# Revit family: PowderCoatRange_Dulux_Duralloy
name_source: partatom
category: Generic Models
revit_build: Autodesk Revit 2018 (Build: 20190510_1515(x64)
units: mm (PartAtom-declared; Revit-internal decimal feet)

## family parameters
Always vertical = Yes
Can host rebar = No
Cut with Voids When Loaded = No
Part Type = Normal
Room Calculation Point = No
Round Connector Dimension = Use Diameter
Shared = No
Work Plane-Based = No

## types (1)
- PowderCoatRange_Dulux_Duralloy
    Manufacturer = Dulux
    Material0001 = PowderCoat_Dulux_Duralloy_Almond_Matt
    Material0002 = PowderCoat_Dulux_Duralloy_ApplianceWhite_Matt
    Material0003 = PowderCoat_Dulux_Duralloy_Aquarium_Matt
    Material0004 = PowderCoat_Dulux_Duralloy_ArcticWhite_Satin
    Material0005 = PowderCoat_Dulux_Duralloy_Azure_Matt
    Material0006 = PowderCoat_Dulux_Duralloy_BlueFin_Matt
    Material0007 = PowderCoat_Dulux_Duralloy_Blueseye_Matt
    Material0008 = PowderCoat_Dulux_Duralloy_BondRivergum_Matt
    Material0009 = PowderCoat_Dulux_Duralloy_BoneWhite_Matt
    Material0010 = PowderCoat_Dulux_Duralloy_Bronco_Matt
    Material0011 = PowderCoat_Dulux_Duralloy_CanvasCloth_Matt
    Material0012 = PowderCoat_Dulux_Duralloy_ChampagneKinetic_Matt
    Material0013 = PowderCoat_Dulux_Duralloy_ChampersKinetic_Matt
    Material0014 = PowderCoat_Dulux_Duralloy_Charcoal_Matt
    Material0015 = PowderCoat_Dulux_Duralloy_ColaRed_Satin
    Material0016 = PowderCoat_Dulux_Duralloy_CopperMetallicKinetic_Satin
    Material0017 = PowderCoat_Dulux_Duralloy_DeepTeal_Matt
    Material0018 = PowderCoat_Dulux_Duralloy_DesertSand_Matt
    Material0019 = PowderCoat_Dulux_Duralloy_Dijon_Matt
    Material0020 = PowderCoat_Dulux_Duralloy_Flaxpod_Matt
    Material0021 = PowderCoat_Dulux_Duralloy_Flint_Matt
    Material0022 = PowderCoat_Dulux_Duralloy_GhostGrey_Matt
    Material0023 = PowderCoat_Dulux_Duralloy_Gravel_Matt
    Material0024 = PowderCoat_Dulux_Duralloy_GreyFriars_Matt
    Material0025 = PowderCoat_Dulux_Duralloy_GullGrey_Matt
    Material0026 = PowderCoat_Dulux_Duralloy_GunmetalMetallicKinetic_Satin
    Material0027 = PowderCoat_Dulux_Duralloy_IndigoBlue_Matt
    Material0028 = PowderCoat_Dulux_Duralloy_Ironsand_Matt
    Material0029 = PowderCoat_Dulux_Duralloy_Jay_Matt
    Material0030 = PowderCoat_Dulux_Duralloy_Karaka_Matt
    Material0031 = PowderCoat_Dulux_Duralloy_Kauri_Matt
    Material0032 = PowderCoat_Dulux_Duralloy_Kodiak_Matt
    Material0033 = PowderCoat_Dulux_Duralloy_Lichen_Matt
    Material0034 = PowderCoat_Dulux_Duralloy_Lignite_Matt
    Material0035 = PowderCoat_Dulux_Duralloy_Magnolia_Matt
    Material0036 = PowderCoat_Dulux_Duralloy_MannexApplianceWhite_Matt
    Material0037 = PowderCoat_Dulux_Duralloy_MannexBronco_Matt
    Material0038 = PowderCoat_Dulux_Duralloy_MannexCharcoal_Matt
    Material0039 = PowderCoat_Dulux_Duralloy_MannexGreyFriars_Matt
    Material0040 = PowderCoat_Dulux_Duralloy_MannexIronsand_Matt
    Material0041 = PowderCoat_Dulux_Duralloy_MannexBlack_Matt
    Material0042 = PowderCoat_Dulux_Duralloy_MannexMetroSilverPearl_Matt
    Material0043 = PowderCoat_Dulux_Duralloy_MannexSandstoneGrey_Matt
    Material0044 = PowderCoat_Dulux_Duralloy_MannexTitania_Matt
    Material0045 = PowderCoat_Dulux_Duralloy_Black_Matt
    Material0046 = PowderCoat_Dulux_Duralloy_MetropolisCoalDustKinetic_Matt
    Material0047 = PowderCoat_Dulux_Duralloy_MetropolisElectricCowKinetic_Matt
    Material0048 = PowderCoat_Dulux_Duralloy_MetropolisSilverPearlKinetic_Satin
    Material0049 = PowderCoat_Dulux_Duralloy_MetropolisWarmWhitePearlKinetic_Satin
    Material0050 = PowderCoat_Dulux_Duralloy_MidGrey_Matt
    Material0051 = PowderCoat_Dulux_Duralloy_MineralBrownKinetic_Satin
    Material0052 = PowderCoat_Dulux_Duralloy_MistGreen_Matt
    Material0053 = PowderCoat_Dulux_Duralloy_Navy_Matt
    Material0054 = PowderCoat_Dulux_Duralloy_NewDenimBlue_Matt
    Material0055 = PowderCoat_Dulux_Duralloy_Oceans12Kinetic_Satin
    Material0056 = PowderCoat_Dulux_Duralloy_OffWhite_Matt
    Material0057 = PowderCoat_Dulux_Duralloy_O'KeefeGrey_Matt
    Material0058 = PowderCoat_Dulux_Duralloy_Olive_Matt
    Material0059 = PowderCoat_Dulux_Duralloy_PermanentGreen_Matt
    Material0060 = PowderCoat_Dulux_Duralloy_PioneerRed_Matt
    Material0061 = PowderCoat_Dulux_Duralloy_PlatypusKinetic_Satin
    Material0062 = PowderCoat_Dulux_Duralloy_Pohutukawa_Matt
    Material0063 = PowderCoat_Dulux_Duralloy_Pounamu_Matt
    Material0064 = PowderCoat_Dulux_Duralloy_RangoonGreen_Matt
    Material0065 = PowderCoat_Dulux_Duralloy_RivergumBeige_Matt
    Material0066 = PowderCoat_Dulux_Duralloy_SandstoneGrey_Matt
    Material0067 = PowderCoat_Dulux_Duralloy_Black_Satin
    Material0068 = PowderCoat_Dulux_Duralloy_Scoria_Matt
    Material0069 = PowderCoat_Dulux_Duralloy_SilverStarKinetic_Satin
    Material0070 = PowderCoat_Dulux_Duralloy_SlateBlue_Matt
    Material0071 = PowderCoat_Dulux_Duralloy_SmoothCream_Matt
    Material0072 = PowderCoat_Dulux_Duralloy_Sorrell_Matt
    Material0073 = PowderCoat_Dulux_Duralloy_StElmosFireKinetic_Satin
    Material0074 = PowderCoat_Dulux_Duralloy_Stone_Matt
    Material0075 = PowderCoat_Dulux_Duralloy_StormBlue_Matt
    Material0076 = PowderCoat_Dulux_Duralloy_Stromboli_Matt
    Material0077 = PowderCoat_Dulux_Duralloy_Terracotta_Matt
    Material0078 = PowderCoat_Dulux_Duralloy_ThunderGrey_Matt
    Material0079 = PowderCoat_Dulux_Duralloy_Titania_Matt
    Material0080 = PowderCoat_Dulux_Duralloy_Tomcat_Matt
    Material0081 = PowderCoat_Dulux_Duralloy_TransformerGrey_Matt
    Material0082 = PowderCoat_Dulux_Duralloy_TuataraKintetic_Satin
    Material0083 = PowderCoat_Dulux_Duralloy_TuskTusk_Matt
    Material0084 = PowderCoat_Dulux_Duralloy_Wasp_Matt
    Material0085 = PowderCoat_Dulux_Duralloy_Wedgewood_Matt
    Material0086 = PowderCoat_Dulux_Duralloy_WindowBronzeKinetic_Matt
    Material0087 = PowderCoat_Dulux_Duralloy_Wizard_Matt
    Material0088 = PowderCoat_Dulux_Duralloy_Woodwind_Matt
    Material0089 = <By Category>
    Material0090 = <By Category>
    Material0091 = <By Category>
    Material0092 = <By Category>
    Material0093 = <By Category>
    Material0094 = <By Category>
    Material0095 = <By Category>
    Material0096 = <By Category>
    Material0097 = <By Category>
    Material0098 = <By Category>
    Material0099 = <By Category>
    Material0100 = <By Category>
    Material0101 = <By Category>
    Material0102 = <By Category>
    Material0103 = <By Category>
    Material0104 = <By Category>
    Material0105 = <By Category>
    Material0106 = <By Category>
    Material0107 = <By Category>
    Material0108 = <By Category>
    Material0109 = <By Category>
    Material0110 = <By Category>
    Material0111 = <By Category>
    Material0112 = <By Category>
    Material0113 = <By Category>
    Material0114 = <By Category>
    Material0115 = <By Category>
    Material0116 = <By Category>
    Material0117 = <By Category>
    Material0118 = <By Category>
    Material0119 = <By Category>
    Material0120 = <By Category>
    Material0121 = <By Category>
    Material0122 = <By Category>
    Material0123 = <By Category>
    Material0124 = <By Category>
    Material0125 = <By Category>
    Material0126 = <By Category>
    Material0127 = <By Category>
    Material0128 = <By Category>
    Material0129 = <By Category>
    Material0130 = <By Category>
    Material0131 = <By Category>
    Material0132 = <By Category>
    Material0133 = <By Category>
    Material0134 = <By Category>
    Material0135 = <By Category>
    Material0136 = <By Category>
    Material0137 = <By Category>
    Material0138 = <By Category>
    Material0139 = <By Category>
    Material0140 = <By Category>
    Material0141 = <By Category>
    Material0142 = <By Category>
    Material0143 = <By Category>
    Material0144 = <By Category>
    Material0145 = <By Category>
    Material0146 = <By Category>
    Material0147 = <By Category>
    Material0148 = <By Category>
    Material0149 = <By Category>
    Material0150 = <By Category>
    Material0151 = <By Category>
    Material0152 = <By Category>
    Material0153 = <By Category>
    Material0154 = <By Category>
    Material0155 = <By Category>
    Material0156 = <By Category>
    Material0157 = <By Category>
    Material0158 = <By Category>
    Material0159 = <By Category>
    Material0160 = <By Category>
    Material0161 = <By Category>
    Material0162 = <By Category>
    Material0163 = <By Category>
    Material0164 = <By Category>
    Material0165 = <By Category>
    Material0166 = <By Category>
    Material0167 = <By Category>
    Material0168 = <By Category>
    Material0169 = <By Category>
    Material0170 = <By Category>
    Material0171 = <By Category>
    Material0172 = <By Category>
    Material0173 = <By Category>
    Material0174 = <By Category>
    Material0175 = <By Category>
    Material0176 = <By Category>
    Material0177 = <By Category>
    Material0178 = <By Category>
    Material0179 = <By Category>
    Material0180 = <By Category>
    Material0181 = <By Category>
    Material0182 = <By Category>
    Material0183 = <By Category>
    Material0184 = <By Category>
    Material0185 = <By Category>
    Material0186 = <By Category>
    Material0187 = <By Category>
    Material0188 = <By Category>
    Material0189 = <By Category>
    Material0190 = <By Category>
    Material0191 = <By Category>
    Material0192 = <By Category>
    Material0193 = <By Category>
    Material0194 = <By Category>
    Material0195 = <By Category>
    Material0196 = <By Category>
    Material0197 = <By Category>
    Material0198 = <By Category>
    Material0199 = <By Category>
    Material0200 = <By Category>
    Material0201 = <By Category>
    Material0202 = <By Category>
    Material0203 = <By Category>
    Material0204 = <By Category>
    Material0205 = <By Category>
    Material0206 = <By Category>
    Material0207 = <By Category>
    Material0208 = <By Category>
    Material0209 = <By Category>
    Material0210 = <By Category>
    Material0211 = <By Category>
    Material0212 = <By Category>
    Material0213 = <By Category>
    Material0214 = <By Category>
    Material0215 = <By Category>
    Material0216 = <By Category>
    Material0217 = <By Category>
    Material0218 = <By Category>
    Material0219 = <By Category>
    Material0220 = <By Category>
    Material0221 = <By Category>
    Material0222 = <By Category>
    Material0223 = <By Category>
    Material0224 = <By Category>
    Material0225 = <By Category>
    Material0226 = <By Category>
    Material0227 = <By Category>
    Material0228 = <By Category>
    Material0229 = <By Category>
    Material0230 = <By Category>
    Material0231 = <By Category>
    Material0232 = <By Category>
    Material0233 = <By Category>
    Material0234 = <By Category>
    Material0235 = <By Category>
    Material0236 = <By Category>
    Material0237 = <By Category>
    Material0238 = <By Category>
    Material0239 = <By Category>
    Material0240 = <By Category>
    Material0241 = <By Category>
    Material0242 = <By Category>
    Material0243 = <By Category>
    Material0244 = <By Category>
    Material0245 = <By Category>
    Material0246 = <By Category>
    Material0247 = <By Category>
    Material0248 = <By Category>
    Material0249 = <By Category>
    Material0250 = <By Category>
    Material0251 = <By Category>
    Material0252 = <By Category>
    Material0253 = <By Category>
    Material0254 = <By Category>
    Material0255 = <By Category>
    Material0256 = <By Category>
    Material0257 = <By Category>
    Material0258 = <By Category>
    Material0259 = <By Category>
    Material0260 = <By Category>
    Material0261 = <By Category>
    Material0262 = <By Category>
    Material0263 = <By Category>
    Material0264 = <By Category>
    Material0265 = <By Category>
    Material0266 = <By Category>
    Material0267 = <By Category>
    Material0268 = <By Category>
    Material0269 = <By Category>
    Material0270 = <By Category>
    Material0271 = <By Category>
    Material0272 = <By Category>
    Material0273 = <By Category>
    Material0274 = <By Category>
    Material0275 = <By Category>
    Material0276 = <By Category>
    Material0277 = <By Category>
    Material0278 = <By Category>
    Material0279 = <By Category>
    Material0280 = <By Category>
    Material0281 = <By Category>
    Material0282 = <By Category>
    Material0283 = <By Category>
    Material0284 = <By Category>
    Material0285 = <By Category>
    Material0286 = <By Category>
    Material0287 = <By Category>
    Material0288 = <By Category>
    Material0289 = <By Category>
    Material0290 = <By Category>
    Material0291 = <By Category>
    Material0292 = <By Category>
    Material0293 = <By Category>
    Material0294 = <By Category>
    Material0295 = <By Category>
    Material0296 = <By Category>
    Material0297 = <By Category>
    Material0298 = <By Category>
    Material0299 = <By Category>
    Material0300 = <By Category>
    Material0301 = <By Category>
    Material0302 = <By Category>
    Material0303 = <By Category>
    Material0304 = <By Category>
    Material0305 = <By Category>
    Material0306 = <By Category>
    Material0307 = <By Category>
    Material0308 = <By Category>
    Material0309 = <By Category>
    Material0310 = <By Category>
    Material0311 = <By Category>
    Material0312 = <By Category>
    Material0313 = <By Category>
    Material0314 = <By Category>
    Material0315 = <By Category>
    Material0316 = <By Category>
    Material0317 = <By Category>
    Material0318 = <By Category>
    Material0319 = <By Category>
    Material0320 = <By Category>
    Material0321 = <By Category>
    Material0322 = <By Category>
    Material0323 = <By Category>
    Material0324 = <By Category>
    Material0325 = <By Category>
    Material0326 = <By Category>
    Material0327 = <By Category>
    Material0328 = <By Category>
    Material0329 = <By Category>
    Material0330 = <By Category>
    Material0331 = <By Category>
    Material0332 = <By Category>
    Material0333 = <By Category>
    Material0334 = <By Category>
    Material0335 = <By Category>
    Material0336 = <By Category>
    Material0337 = <By Category>
    Material0338 = <By Category>
    Material0339 = <By Category>
    Material0340 = <By Category>
    Material0341 = <By Category>
    Material0342 = <By Category>
    Material0343 = <By Category>
    Material0344 = <By Category>
    Material0345 = <By Category>
    Material0346 = <By Category>
    Material0347 = <By Category>
    Material0348 = <By Category>
    Material0349 = <By Category>
    Material0350 = <By Category>
    Material0351 = <By Category>
    Material0352 = <By Category>
    Material0353 = <By Category>
    Material0354 = <By Category>
    Material0355 = <By Category>
    Material0356 = <By Category>
    Material0357 = <By Category>
    Material0358 = <By Category>
    Material0359 = <By Category>
    Material0360 = <By Category>
    Material0361 = <By Category>
    Material0362 = <By Category>
    Material0363 = <By Category>
    Material0364 = <By Category>
    Material0365 = <By Category>
    Material0366 = <By Category>
    Material0367 = <By Category>
    Material0368 = <By Category>
    Material0369 = <By Category>
    Material0370 = <By Category>
    Material0371 = <By Category>
    Material0372 = <By Category>
    Material0373 = <By Category>
    Material0374 = <By Category>
    Material0375 = <By Category>
    Material0376 = <By Category>
    Material0377 = <By Category>
    Material0378 = <By Category>
    Material0379 = <By Category>
    Material0380 = <By Category>
    Material0381 = <By Category>
    Material0382 = <By Category>
    Material0383 = <By Category>
    Material0384 = <By Category>
    Material0385 = <By Category>
    Material0386 = <By Category>
    Material0387 = <By Category>
    Material0388 = <By Category>
    Material0389 = <By Category>
    Material0390 = <By Category>
    Material0391 = <By Category>
    Material0392 = <By Category>
    Material0393 = <By Category>
    Material0394 = <By Category>
    Material0395 = <By Category>
    Material0396 = <By Category>
    Material0397 = <By Category>
    Material0398 = <By Category>
    Material0399 = <By Category>
    Material0400 = <By Category>
    Material0401 = <By Category>
    Material0402 = <By Category>
    Material0403 = <By Category>
    Material0404 = <By Category>
    Material0405 = <By Category>
    Material0406 = <By Category>
    Material0407 = <By Category>
    Material0408 = <By Category>
    Material0409 = <By Category>
    Material0410 = <By Category>
    Material0411 = <By Category>
    Material0412 = <By Category>
    Material0413 = <By Category>
    Material0414 = <By Category>
    Material0415 = <By Category>
    Material0416 = <By Category>
    Material0417 = <By Category>
    Material0418 = <By Category>
    Material0419 = <By Category>
    Material0420 = <By Category>
    Material0421 = <By Category>
    Material0422 = <By Category>
    Material0423 = <By Category>
    Material0424 = <By Category>
    Material0425 = <By Category>
    Material0426 = <By Category>
    Material0427 = <By Category>
    Material0428 = <By Category>
    Material0429 = <By Category>
    Material0430 = <By Category>
    Material0431 = <By Category>
    Material0432 = <By Category>
    Material0433 = <By Category>
    Material0434 = <By Category>
    Material0435 = <By Category>
    Material0436 = <By Category>
    Material0437 = <By Category>
    Material0438 = <By Category>
    Material0439 = <By Category>
    Material0440 = <By Category>
    Material0441 = <By Category>
    Material0442 = <By Category>
    Material0443 = <By Category>
    Material0444 = <By Category>
    Material0445 = <By Category>
    Material0446 = <By Category>
    Material0447 = <By Category>
    Material0448 = <By Category>
    Material0449 = <By Category>
    Material0450 = <By Category>
    Material0451 = <By Category>
    Material0452 = <By Category>
    Material0453 = <By Category>
    Material0454 = <By Category>
    Material0455 = <By Category>
    Material0456 = <By Category>
    Material0457 = <By Category>
    Material0458 = <By Category>
    Material0459 = <By Category>
    Material0460 = <By Category>
    Material0461 = <By Category>
    Material0462 = <By Category>
    Material0463 = <By Category>
    Material0464 = <By Category>
    Material0465 = <By Category>
    Material0466 = <By Category>
    Material0467 = <By Category>
    Material0468 = <By Category>
    Material0469 = <By Category>
    Material0470 = <By Category>
    Material0471 = <By Category>
    Material0472 = <By Category>
    Material0473 = <By Category>
    Material0474 = <By Category>
    Material0475 = <By Category>
    Material0476 = <By Category>
    Material0477 = <By Category>
    Material0478 = <By Category>
    Material0479 = <By Category>
    Material0480 = <By Category>
    Material0481 = <By Category>
    Material0482 = <By Category>
    Material0483 = <By Category>
    Material0484 = <By Category>
    Material0485 = <By Category>
    Material0486 = <By Category>
    Material0487 = <By Category>
    Material0488 = <By Category>
    Material0489 = <By Category>
    Material0490 = <By Category>
    Material0491 = <By Category>
    Material0492 = <By Category>
    Material0493 = <By Category>
    Material0494 = <By Category>
    Material0495 = <By Category>
    Material0496 = <By Category>
    Material0497 = <By Category>
    Material0498 = <By Category>
    Material0499 = <By Category>
    Material0500 = <By Category>
    Material0501 = <By Category>
    Material0502 = <By Category>
    Material0503 = <By Category>
    Material0504 = <By Category>
    Material0505 = <By Category>
    Material0506 = <By Category>
    Material0507 = <By Category>
    Material0508 = <By Category>
    Material0509 = <By Category>
    Material0510 = <By Category>
    Material0511 = <By Category>
    Material0512 = <By Category>
    Material0513 = <By Category>
    Material0514 = <By Category>
    Material0515 = <By Category>
    Material0516 = <By Category>
    Material0517 = <By Category>
    Material0518 = <By Category>
    Material0519 = <By Category>
    Material0520 = <By Category>
    Material0521 = <By Category>
    Material0522 = <By Category>
    Material0523 = <By Category>
    Material0524 = <By Category>
    Material0525 = <By Category>
    Material0526 = <By Category>
    Material0527 = <By Category>
    Material0528 = <By Category>
    Material0529 = <By Category>
    Material0530 = <By Category>
    Material0531 = <By Category>
    Material0532 = <By Category>
    Material0533 = <By Category>
    Material0534 = <By Category>
    Material0535 = <By Category>
    Material0536 = <By Category>
    Material0537 = <By Category>
    Material0538 = <By Category>
    Material0539 = <By Category>
    Material0540 = <By Category>
    Material0541 = <By Category>
    Material0542 = <By Category>
    Material0543 = <By Category>
    Material0544 = <By Category>
    Material0545 = <By Category>
    Material0546 = <By Category>
    Material0547 = <By Category>
    Material0548 = <By Category>
    Material0549 = <By Category>
    Material0550 = <By Category>
    Material0551 = <By Category>
    Material0552 = <By Category>
    Material0553 = <By Category>
    Material0554 = <By Category>
    Material0555 = <By Category>
    Material0556 = <By Category>
    Material0557 = <By Category>
    Material0558 = <By Category>
    Material0559 = <By Category>
    Material0560 = <By Category>
    Material0561 = <By Category>
    Material0562 = <By Category>
    Material0563 = <By Category>
    Material0564 = <By Category>
    Material0565 = <By Category>
    Material0566 = <By Category>
    Material0567 = <By Category>
    Material0568 = <By Category>
    Material0569 = <By Category>
    Material0570 = <By Category>
    Material0571 = <By Category>
    Material0572 = <By Category>
    Material0573 = <By Category>
    Material0574 = <By Category>
    Material0575 = <By Category>
    Material0576 = <By Category>
    Material0577 = <By Category>
    Material0578 = <By Category>
    Material0579 = <By Category>
    Material0580 = <By Category>
    Material0581 = <By Category>
    Material0582 = <By Category>
    Material0583 = <By Category>
    Material0584 = <By Category>
    Material0585 = <By Category>
    Material0586 = <By Category>
    Material0587 = <By Category>
    Material0588 = <By Category>
    Material0589 = <By Category>
    Material0590 = <By Category>
    Material0591 = <By Category>
    Material0592 = <By Category>
    Material0593 = <By Category>
    Material0594 = <By Category>
    Material0595 = <By Category>
    Material0596 = <By Category>
    Material0597 = <By Category>
    Material0598 = <By Category>
    Material0599 = <By Category>
    Material0600 = <By Category>
    Material0601 = <By Category>
    Material0602 = <By Category>
    Material0603 = <By Category>
    Material0604 = <By Category>
    Material0605 = <By Category>
    Material0606 = <By Category>
    Material0607 = <By Category>
    Material0608 = <By Category>
    Material0609 = <By Category>
    Material0610 = <By Category>
    Material0611 = <By Category>
    Material0612 = <By Category>
    Material0613 = <By Category>
    Material0614 = <By Category>
    Material0615 = <By Category>
    Material0616 = <By Category>
    Material0617 = <By Category>
    Material0618 = <By Category>
    Material0619 = <By Category>
    Material0620 = <By Category>
    Material0621 = <By Category>
    Material0622 = <By Category>
    Material0623 = <By Category>
    Material0624 = <By Category>
    Material0625 = <By Category>
    Material0626 = <By Category>
    Material0627 = <By Category>
    Material0628 = <By Category>
    Material0629 = <By Category>
    Material0630 = <By Category>
    Material0631 = <By Category>
    Material0632 = <By Category>
    Material0633 = <By Category>
    Material0634 = <By Category>
    Material0635 = <By Category>
    Material0636 = <By Category>
    Material0637 = <By Category>
    Material0638 = <By Category>
    Material0639 = <By Category>
    Material0640 = <By Category>
    Material0641 = <By Category>
    Material0642 = <By Category>
    Material0643 = <By Category>
    Material0644 = <By Category>
    Material0645 = <By Category>
    Material0646 = <By Category>
    Material0647 = <By Category>
    Material0648 = <By Category>
    Material0649 = <By Category>
    Material0650 = <By Category>
    Material0651 = <By Category>
    Material0652 = <By Category>
    Material0653 = <By Category>
    Material0654 = <By Category>
    Material0655 = <By Category>
    Material0656 = <By Category>
    Material0657 = <By Category>
    Material0658 = <By Category>
    Material0659 = <By Category>
    Material0660 = <By Category>
    Material0661 = <By Category>
    Material0662 = <By Category>
    Material0663 = <By Category>
    Material0664 = <By Category>
    Material0665 = <By Category>
    Material0666 = <By Category>
    Material0667 = <By Category>
    Material0668 = <By Category>
    Material0669 = <By Category>
    Material0670 = <By Category>
    Material0671 = <By Category>
    Material0672 = <By Category>
    Material0673 = <By Category>
    Material0674 = <By Category>
    Material0675 = <By Category>
    Material0676 = <By Category>
    Material0677 = <By Category>
    Material0678 = <By Category>
    Material0679 = <By Category>
    Material0680 = <By Category>
    Material0681 = <By Category>
    Material0682 = <By Category>
    Material0683 = <By Category>
    Material0684 = <By Category>
    Material0685 = <By Category>
    Material0686 = <By Category>
    Material0687 = <By Category>
    Material0688 = <By Category>
    Material0689 = <By Category>
    Material0690 = <By Category>
    Material0691 = <By Category>
    Material0692 = <By Category>
    Material0693 = <By Category>
    Material0694 = <By Category>
    Material0695 = <By Category>
    Material0696 = <By Category>
    Material0697 = <By Category>
    Material0698 = <By Category>
    Material0699 = <By Category>
    Material0700 = <By Category>
    Material0701 = <By Category>
    Material0702 = <By Category>
    Material0703 = <By Category>
    Material0704 = <By Category>
    Material0705 = <By Category>
    Material0706 = <By Category>
    Material0707 = <By Category>
    Material0708 = <By Category>
    Material0709 = <By Category>
    Material0710 = <By Category>
    Material0711 = <By Category>
    Material0712 = <By Category>
    Material0713 = <By Category>
    Material0714 = <By Category>
    Material0715 = <By Category>
    Material0716 = <By Category>
    Material0717 = <By Category>
    Material0718 = <By Category>
    Material0719 = <By Category>
    Material0720 = <By Category>
    Material0721 = <By Category>
    Material0722 = <By Category>
    Material0723 = <By Category>
    Material0724 = <By Category>
    Material0725 = <By Category>
    Material0726 = <By Category>
    Material0727 = <By Category>
    Material0728 = <By Category>
    Material0729 = <By Category>
    Material0730 = <By Category>
    Material0731 = <By Category>
    Material0732 = <By Category>
    Material0733 = <By Category>
    Material0734 = <By Category>
    Material0735 = <By Category>
    Material0736 = <By Category>
    Material0737 = <By Category>
    Material0738 = <By Category>
    Material0739 = <By Category>
    Material0740 = <By Category>
    Material0741 = <By Category>
    Material0742 = <By Category>
    Material0743 = <By Category>
    Material0744 = <By Category>
    Material0745 = <By Category>
    Material0746 = <By Category>
    Material0747 = <By Category>
    Material0748 = <By Category>
    Material0749 = <By Category>
    Material0750 = <By Category>
    Material0751 = <By Category>
    Material0752 = <By Category>
    Material0753 = <By Category>
    Material0754 = <By Category>
    Material0755 = <By Category>
    Material0756 = <By Category>
    Material0757 = <By Category>
    Material0758 = <By Category>
    Material0759 = <By Category>
    Material0760 = <By Category>
    Material0761 = <By Category>
    Material0762 = <By Category>
    Material0763 = <By Category>
    Material0764 = <By Category>
    Material0765 = <By Category>
    Material0766 = <By Category>
    Material0767 = <By Category>
    Material0768 = <By Category>
    Material0769 = <By Category>
    Material0770 = <By Category>
    Material0771 = <By Category>
    Material0772 = <By Category>
    Material0773 = <By Category>
    Material0774 = <By Category>
    Material0775 = <By Category>
    Material0776 = <By Category>
    Material0777 = <By Category>
    Material0778 = <By Category>
    Material0779 = <By Category>
    Material0780 = <By Category>
    Material0781 = <By Category>
    Material0782 = <By Category>
    Material0783 = <By Category>
    Material0784 = <By Category>
    Material0785 = <By Category>
    Material0786 = <By Category>
    Material0787 = <By Category>
    Material0788 = <By Category>
    Material0789 = <By Category>
    Material0790 = <By Category>
    Material0791 = <By Category>
    Material0792 = <By Category>
    Material0793 = <By Category>
    Material0794 = <By Category>
    Material0795 = <By Category>
    Material0796 = <By Category>
    Material0797 = <By Category>
    Material0798 = <By Category>
    Material0799 = <By Category>
    Material0800 = <By Category>
    Material0801 = <By Category>
    Material0802 = <By Category>
    Material0803 = <By Category>
    Material0804 = <By Category>
    Material0805 = <By Category>
    Material0806 = <By Category>
    Material0807 = <By Category>
    Material0808 = <By Category>
    Material0809 = <By Category>
    Material0810 = <By Category>
    Material0811 = <By Category>
    Material0812 = <By Category>
    Material0813 = <By Category>
    Material0814 = <By Category>
    Material0815 = <By Category>
    Material0816 = <By Category>
    Material0817 = <By Category>
    Material0818 = <By Category>
    Material0819 = <By Category>
    Material0820 = <By Category>
    Material0821 = <By Category>
    Material0822 = <By Category>
    Material0823 = <By Category>
    Material0824 = <By Category>
    Material0825 = <By Category>
    Material0826 = <By Category>
    Material0827 = <By Category>
    Material0828 = <By Category>
    Material0829 = <By Category>
    Material0830 = <By Category>
    Material0831 = <By Category>
    Material0832 = <By Category>
    Material0833 = <By Category>
    Material0834 = <By Category>
    Material0835 = <By Category>
    Material0836 = <By Category>
    Material0837 = <By Category>
    Material0838 = <By Category>
    Material0839 = <By Category>
    Material0840 = <By Category>
    Material0841 = <By Category>
    Material0842 = <By Category>
    Material0843 = <By Category>
    Material0844 = <By Category>
    Material0845 = <By Category>
    Material0846 = <By Category>
    Material0847 = <By Category>
    Material0848 = <By Category>
    Material0849 = <By Category>
    Material0850 = <By Category>
    Material0851 = <By Category>
    Material0852 = <By Category>
    Material0853 = <By Category>
    Material0854 = <By Category>
    Material0855 = <By Category>
    Material0856 = <By Category>
    Material0857 = <By Category>
    Material0858 = <By Category>
    Material0859 = <By Category>
    Material0860 = <By Category>
    Material0861 = <By Category>
    Material0862 = <By Category>
    Material0863 = <By Category>
    Material0864 = <By Category>
    Material0865 = <By Category>
    Material0866 = <By Category>
    Material0867 = <By Category>
    Material0868 = <By Category>
    Material0869 = <By Category>
    Material0870 = <By Category>
    Material0871 = <By Category>
    Material0872 = <By Category>
    Material0873 = <By Category>
    Material0874 = <By Category>
    Material0875 = <By Category>
    Material0876 = <By Category>
    Material0877 = <By Category>
    Material0878 = <By Category>
    Material0879 = <By Category>
    Material0880 = <By Category>
    Material0881 = <By Category>
    Material0882 = <By Category>
    Material0883 = <By Category>
    Material0884 = <By Category>
    Material0885 = <By Category>
    Material0886 = <By Category>
    Material0887 = <By Category>
    Material0888 = <By Category>
    Material0889 = <By Category>
    Material0890 = <By Category>
    Material0891 = <By Category>
    Material0892 = <By Category>
    Material0893 = <By Category>
    Material0894 = <By Category>
    Material0895 = <By Category>
    Material0896 = <By Category>
    Material0897 = <By Category>
    Material0898 = <By Category>
    Material0899 = <By Category>
    Material0900 = <By Category>
    Material0901 = <By Category>
    Material0902 = <By Category>
    Material0903 = <By Category>
    Material0904 = <By Category>
    Material0905 = <By Category>
    Material0906 = <By Category>
    Material0907 = <By Category>
    Material0908 = <By Category>
    Material0909 = <By Category>
    Material0910 = <By Category>
    Material0911 = <By Category>
    Material0912 = <By Category>
    Material0913 = <By Category>
    Material0914 = <By Category>
    Material0915 = <By Category>
    Material0916 = <By Category>
    Material0917 = <By Category>
    Material0918 = <By Category>
    Material0919 = <By Category>
    Material0920 = <By Category>
    Material0921 = <By Category>
    Material0922 = <By Category>
    Material0923 = <By Category>
    Material0924 = <By Category>
    Material0925 = <By Category>
    Material0926 = <By Category>
    Material0927 = <By Category>
    Material0928 = <By Category>
    Material0929 = <By Category>
    Material0930 = <By Category>
    Material0931 = <By Category>
    Material0932 = <By Category>
    Material0933 = <By Category>
    Material0934 = <By Category>
    Material0935 = <By Category>
    Material0936 = <By Category>
    Material0937 = <By Category>
    Material0938 = <By Category>
    Material0939 = <By Category>
    Material0940 = <By Category>
    Material0941 = <By Category>
    Material0942 = <By Category>
    Material0943 = <By Category>
    Material0944 = <By Category>
    Material0945 = <By Category>
    Material0946 = <By Category>
    Material0947 = <By Category>
    Material0948 = <By Category>
    Material0949 = <By Category>
    Material0950 = <By Category>
    Material0951 = <By Category>
    Material0952 = <By Category>
    Material0953 = <By Category>
    Material0954 = <By Category>
    Material0955 = <By Category>
    Material0956 = <By Category>
    Material0957 = <By Category>
    Material0958 = <By Category>
    Material0959 = <By Category>
    Material0960 = <By Category>
    Material0961 = <By Category>
    Material0962 = <By Category>
    Material0963 = <By Category>
    Material0964 = <By Category>
    Material0965 = <By Category>
    Material0966 = <By Category>
    Material0967 = <By Category>
    Material0968 = <By Category>
    Material0969 = <By Category>
    Material0970 = <By Category>
    Material0971 = <By Category>
    Material0972 = <By Category>
    Material0973 = <By Category>
    Material0974 = <By Category>
    Material0975 = <By Category>
    Material0976 = <By Category>
    Material0977 = <By Category>
    Material0978 = <By Category>
    Material0979 = <By Category>
    Material0980 = <By Category>
    Material0981 = <By Category>
    Material0982 = <By Category>
    Material0983 = <By Category>
    Material0984 = <By Category>
    Material0985 = <By Category>
    Material0986 = <By Category>
    Material0987 = <By Category>
    Material0988 = <By Category>
    Material0989 = <By Category>
    Material0990 = <By Category>
    Material0991 = <By Category>
    Material0992 = <By Category>
    Material0993 = <By Category>
    Material0994 = <By Category>
    Material0995 = <By Category>
    Material0996 = <By Category>
    Material0997 = <By Category>
    Material0998 = <By Category>
    Material0999 = <By Category>
    Material1000 = <By Category>
    Material1001 = <By Category>
    Material1002 = <By Category>
    Material1003 = <By Category>
    Material1004 = <By Category>
    Material1005 = <By Category>
    Material1006 = <By Category>
    Material1007 = <By Category>
    Material1008 = <By Category>
    Material1009 = <By Category>
    Material1010 = <By Category>
    Material1011 = <By Category>
    Material1012 = <By Category>
    Material1013 = <By Category>
    Material1014 = <By Category>
    Material1015 = <By Category>
    Material1016 = <By Category>
    Material1017 = <By Category>
    Material1018 = <By Category>
    Material1019 = <By Category>
    Material1020 = <By Category>
    Material1021 = <By Category>
    Material1022 = <By Category>
    Material1023 = <By Category>
    Material1024 = <By Category>
    Material1025 = <By Category>
    Material1026 = <By Category>
    Material1027 = <By Category>
    Material1028 = <By Category>
    Material1029 = <By Category>
    Material1030 = <By Category>
    Material1031 = <By Category>
    Material1032 = <By Category>
    Material1033 = <By Category>
    Material1034 = <By Category>
    Material1035 = <By Category>
    Material1036 = <By Category>
    Material1037 = <By Category>
    Material1038 = <By Category>
    Material1039 = <By Category>
    Material1040 = <By Category>
    Material1041 = <By Category>
    Material1042 = <By Category>
    Material1043 = <By Category>
    Material1044 = <By Category>
    Material1045 = <By Category>
    Material1046 = <By Category>
    Material1047 = <By Category>
    Material1048 = <By Category>
    Material1049 = <By Category>
    Material1050 = <By Category>
    Material1051 = <By Category>
    Material1052 = <By Category>
    Material1053 = <By Category>
    Material1054 = <By Category>
    Material1055 = <By Category>
    Material1056 = <By Category>
    Material1057 = <By Category>
    Material1058 = <By Category>
    Material1059 = <By Category>
    Material1060 = <By Category>
    Material1061 = <By Category>
    Material1062 = <By Category>
    Material1063 = <By Category>
    Material1064 = <By Category>
    Material1065 = <By Category>
    Material1066 = <By Category>
    Material1067 = <By Category>
    Material1068 = <By Category>
    Material1069 = <By Category>
    Material1070 = <By Category>
    Material1071 = <By Category>
    Material1072 = <By Category>
    Material1073 = <By Category>
    Material1074 = <By Category>
    Material1075 = <By Category>
    Material1076 = <By Category>
    Material1077 = <By Category>
    Material1078 = <By Category>
    Material1079 = <By Category>
    Material1080 = <By Category>
    Material1081 = <By Category>
    Material1082 = <By Category>
    Material1083 = <By Category>
    Material1084 = <By Category>
    Material1085 = <By Category>
    Material1086 = <By Category>
    Material1087 = <By Category>
    Material1088 = <By Category>
    Material1089 = <By Category>
    Material1090 = <By Category>
    Material1091 = <By Category>
    Material1092 = <By Category>
    Material1093 = <By Category>
    Material1094 = <By Category>
    Material1095 = <By Category>
    Material1096 = <By Category>
    Material1097 = <By Category>
    Material1098 = <By Category>
    Material1099 = <By Category>
    Material1100 = <By Category>
    Material1101 = <By Category>
    Material1102 = <By Category>
    Material1103 = <By Category>
    Material1104 = <By Category>
    Material1105 = <By Category>
    Material1106 = <By Category>
    Material1107 = <By Category>
    Material1108 = <By Category>
    Material1109 = <By Category>
    Material1110 = <By Category>
    Material1111 = <By Category>
    Material1112 = <By Category>
    Material1113 = <By Category>
    Material1114 = <By Category>
    Material1115 = <By Category>
    Material1116 = <By Category>
    Material1117 = <By Category>
    Material1118 = <By Category>
    Material1119 = <By Category>
    Material1120 = <By Category>
    Material1121 = <By Category>
    Material1122 = <By Category>
    Material1123 = <By Category>
    Material1124 = <By Category>
    Material1125 = <By Category>
    Material1126 = <By Category>
    Material1127 = <By Category>
    Material1128 = <By Category>
    Material1129 = <By Category>
    Material1130 = <By Category>
    Material1131 = <By Category>
    Material1132 = <By Category>
    Material1133 = <By Category>
    Material1134 = <By Category>
    Material1135 = <By Category>
    Material1136 = <By Category>
    Material1137 = <By Category>
    Material1138 = <By Category>
    Material1139 = <By Category>
    Material1140 = <By Category>
    Material1141 = <By Category>
    Material1142 = <By Category>
    Material1143 = <By Category>
    Material1144 = <By Category>
    Material1145 = <By Category>
    Material1146 = <By Category>
    Material1147 = <By Category>
    Material1148 = <By Category>
    Material1149 = <By Category>
    Material1150 = <By Category>
    Material1151 = <By Category>
    Material1152 = <By Category>
    Material1153 = <By Category>
    Material1154 = <By Category>
    Material1155 = <By Category>
    Material1156 = <By Category>
    Material1157 = <By Category>
    Material1158 = <By Category>
    Material1159 = <By Category>
    Material1160 = <By Category>
    Material1161 = <By Category>
    Material1162 = <By Category>
    Material1163 = <By Category>
    Material1164 = <By Category>
    Material1165 = <By Category>
    Material1166 = <By Category>
    Material1167 = <By Category>
    Material1168 = <By Category>
    Material1169 = <By Category>
    Material1170 = <By Category>
    Material1171 = <By Category>
    Material1172 = <By Category>
    Material1173 = <By Category>
    Material1174 = <By Category>
    Material1175 = <By Category>
    Material1176 = <By Category>
    Material1177 = <By Category>
    Material1178 = <By Category>
    Material1179 = <By Category>
    Material1180 = <By Category>
    Material1181 = <By Category>
    Material1182 = <By Category>
    Material1183 = <By Category>
    Material1184 = <By Category>
    Material1185 = <By Category>
    Material1186 = <By Category>
    Material1187 = <By Category>
    Material1188 = <By Category>
    Material1189 = <By Category>
    Material1190 = <By Category>
    Material1191 = <By Category>
    Material1192 = <By Category>
    Material1193 = <By Category>
    Material1194 = <By Category>
    Material1195 = <By Category>
    Material1196 = <By Category>
    Material1197 = <By Category>
    Material1198 = <By Category>
    Material1199 = <By Category>
    Material1200 = <By Category>
    Material1201 = <By Category>
    Material1202 = <By Category>
    Material1203 = <By Category>
    Material1204 = <By Category>
    Material1205 = <By Category>
    Material1206 = <By Category>
    Material1207 = <By Category>
    Material1208 = <By Category>
    Material1209 = <By Category>
    Material1210 = <By Category>
    Material1211 = <By Category>
    Material1212 = <By Category>
    Material1213 = <By Category>
    Material1214 = <By Category>
    Material1215 = <By Category>
    Material1216 = <By Category>
    Material1217 = <By Category>
    Material1218 = <By Category>
    Material1219 = <By Category>
    Material1220 = <By Category>
    Material1221 = <By Category>
    Material1222 = <By Category>
    Material1223 = <By Category>
    Material1224 = <By Category>
    Material1225 = <By Category>
    Material1226 = <By Category>
    Material1227 = <By Category>
    Material1228 = <By Category>
    Material1229 = <By Category>
    Material1230 = <By Category>
    Material1231 = <By Category>
    Material1232 = <By Category>
    Material1233 = <By Category>
    Material1234 = <By Category>
    Material1235 = <By Category>
    Material1236 = <By Category>
    Material1237 = <By Category>
    Material1238 = <By Category>
    Material1239 = <By Category>
    Material1240 = <By Category>
    Material1241 = <By Category>
    Material1242 = <By Category>
    Material1243 = <By Category>
    Material1244 = <By Category>
    Material1245 = <By Category>
    Material1246 = <By Category>
    Material1247 = <By Category>
    Material1248 = <By Category>
    Material1249 = <By Category>
    Material1250 = <By Category>
    Material1251 = <By Category>
    Material1252 = <By Category>
    Material1253 = <By Category>
    Material1254 = <By Category>
    Material1255 = <By Category>
    Material1256 = <By Category>
    Material1257 = <By Category>
    Material1258 = <By Category>
    Material1259 = <By Category>
    Material1260 = <By Category>
    Material1261 = <By Category>
    Material1262 = <By Category>
    Material1263 = <By Category>
    Material1264 = <By Category>
    Material1265 = <By Category>
    Material1266 = <By Category>
    Material1267 = <By Category>
    Material1268 = <By Category>
    Material1269 = <By Category>
    Material1270 = <By Category>
    Material1271 = <By Category>
    Material1272 = <By Category>
    Material1273 = <By Category>
    Material1274 = <By Category>
    Material1275 = <By Category>
    Material1276 = <By Category>
    Material1277 = <By Category>
    Material1278 = <By Category>
    Material1279 = <By Category>
    Material1280 = <By Category>
    Material1281 = <By Category>
    Material1282 = <By Category>
    Material1283 = <By Category>
    Material1284 = <By Category>
    Material1285 = <By Category>
    Material1286 = <By Category>
    Material1287 = <By Category>
    Material1288 = <By Category>
    Material1289 = <By Category>
    Material1290 = <By Category>
    Material1291 = <By Category>
    Material1292 = <By Category>
    Material1293 = <By Category>
    Material1294 = <By Category>
    Material1295 = <By Category>
    Material1296 = <By Category>
    Material1297 = <By Category>
    Material1298 = <By Category>
    Material1299 = <By Category>
    Material1300 = <By Category>
    Material1301 = <By Category>
    Material1302 = <By Category>
    Material1303 = <By Category>
    Material1304 = <By Category>
    Material1305 = <By Category>
    Material1306 = <By Category>
    Material1307 = <By Category>
    Material1308 = <By Category>
    Material1309 = <By Category>
    Material1310 = <By Category>
    Material1311 = <By Category>
    Material1312 = <By Category>
    Material1313 = <By Category>
    Material1314 = <By Category>
    Material1315 = <By Category>
    Material1316 = <By Category>
    Material1317 = <By Category>
    Material1318 = <By Category>
    Material1319 = <By Category>
    Material1320 = <By Category>
    Material1321 = <By Category>
    Material1322 = <By Category>
    Material1323 = <By Category>
    Material1324 = <By Category>
    Material1325 = <By Category>
    Material1326 = <By Category>
    Material1327 = <By Category>
    Material1328 = <By Category>
    Material1329 = <By Category>
    Material1330 = <By Category>
    Material1331 = <By Category>
    Material1332 = <By Category>
    Material1333 = <By Category>
    Material1334 = <By Category>
    Material1335 = <By Category>
    Material1336 = <By Category>
    Material1337 = <By Category>
    Material1338 = <By Category>
    Material1339 = <By Category>
    Material1340 = <By Category>
    Material1341 = <By Category>
    Material1342 = <By Category>
    Material1343 = <By Category>
    Material1344 = <By Category>
    Material1345 = <By Category>
    Material1346 = <By Category>
    Material1347 = <By Category>
    Material1348 = <By Category>
    Material1349 = <By Category>
    Material1350 = <By Category>
    Material1351 = <By Category>
    Material1352 = <By Category>
    Material1353 = <By Category>
    Material1354 = <By Category>
    Material1355 = <By Category>
    Material1356 = <By Category>
    Material1357 = <By Category>
    Material1358 = <By Category>
    Material1359 = <By Category>
    Material1360 = <By Category>
    Material1361 = <By Category>
    Material1362 = <By Category>
    Material1363 = <By Category>
    Material1364 = <By Category>
    Material1365 = <By Category>
    Material1366 = <By Category>
    Material1367 = <By Category>
    Material1368 = <By Category>
    Material1369 = <By Category>
    Material1370 = <By Category>
    Material1371 = <By Category>
    Material1372 = <By Category>
    Material1373 = <By Category>
    Material1374 = <By Category>
    Material1375 = <By Category>
    Material1376 = <By Category>
    Material1377 = <By Category>
    Material1378 = <By Category>
    Material1379 = <By Category>
    Material1380 = <By Category>
    Material1381 = <By Category>
    Material1382 = <By Category>
    Material1383 = <By Category>
    Material1384 = <By Category>
    Material1385 = <By Category>
    Material1386 = <By Category>
    Material1387 = <By Category>
    Material1388 = <By Category>
    Material1389 = <By Category>
    Material1390 = <By Category>
    Material1391 = <By Category>
    Material1392 = <By Category>
    Material1393 = <By Category>
    Material1394 = <By Category>
    Material1395 = <By Category>
    Material1396 = <By Category>
    Material1397 = <By Category>
    Material1398 = <By Category>
    Material1399 = <By Category>
    Material1400 = <By Category>
    Material1401 = <By Category>
    Material1402 = <By Category>
    Material1403 = <By Category>
    Material1404 = <By Category>
    Material1405 = <By Category>
    Material1406 = <By Category>
    Material1407 = <By Category>
    Material1408 = <By Category>
    Material1409 = <By Category>
    Material1410 = <By Category>
    Material1411 = <By Category>
    Material1412 = <By Category>
    Material1413 = <By Category>
    Material1414 = <By Category>
    Material1415 = <By Category>
    Material1416 = <By Category>
    Material1417 = <By Category>
    Material1418 = <By Category>
    Material1419 = <By Category>
    Material1420 = <By Category>
    Material1421 = <By Category>
    Material1422 = <By Category>
    Material1423 = <By Category>
    Material1424 = <By Category>
    Material1425 = <By Category>
    Material1426 = <By Category>
    Material1427 = <By Category>
    Material1428 = <By Category>
    Material1429 = <By Category>
    Material1430 = <By Category>
    Material1431 = <By Category>
    Material1432 = <By Category>
    Material1433 = <By Category>
    Material1434 = <By Category>
    Material1435 = <By Category>
    Material1436 = <By Category>
    Material1437 = <By Category>
    Material1438 = <By Category>
    Material1439 = <By Category>
    Material1440 = <By Category>
    Material1441 = <By Category>
    Material1442 = <By Category>
    Material1443 = <By Category>
    Material1444 = <By Category>
    Material1445 = <By Category>
    Material1446 = <By Category>
    Material1447 = <By Category>
    Material1448 = <By Category>
    Material1449 = <By Category>
    Material1450 = <By Category>
    Material1451 = <By Category>
    Material1452 = <By Category>
    Material1453 = <By Category>
    Material1454 = <By Category>
    Material1455 = <By Category>
    Material1456 = <By Category>
    Material1457 = <By Category>
    Material1458 = <By Category>
    Material1459 = <By Category>
    Material1460 = <By Category>
    Material1461 = <By Category>
    Material1462 = <By Category>
    Material1463 = <By Category>
    Material1464 = <By Category>
    Material1465 = <By Category>
    Material1466 = <By Category>
    Material1467 = <By Category>
    Material1468 = <By Category>
    Material1469 = <By Category>
    Material1470 = <By Category>
    Material1471 = <By Category>
    Material1472 = <By Category>
    Material1473 = <By Category>
    Material1474 = <By Category>
    Material1475 = <By Category>
    Material1476 = <By Category>
    Material1477 = <By Category>
    Material1478 = <By Category>
    Material1479 = <By Category>
    Material1480 = <By Category>
    Material1481 = <By Category>
    Material1482 = <By Category>
    Material1483 = <By Category>
    Material1484 = <By Category>
    Material1485 = <By Category>
    Material1486 = <By Category>
    Material1487 = <By Category>
    Material1488 = <By Category>
    Material1489 = <By Category>
    Material1490 = <By Category>
    Material1491 = <By Category>
    Material1492 = <By Category>
    Material1493 = <By Category>
    Material1494 = <By Category>
    Material1495 = <By Category>
    Material1496 = <By Category>
    Material1497 = <By Category>
    Material1498 = <By Category>
    Material1499 = <By Category>
    Material1500 = <By Category>
    Type Comments = Duralloy
    URL = https://www.dulux.com.au

## geometry (parser evidence)
native form markers: Sweep x3
no freeform markers — native parametric forms only
